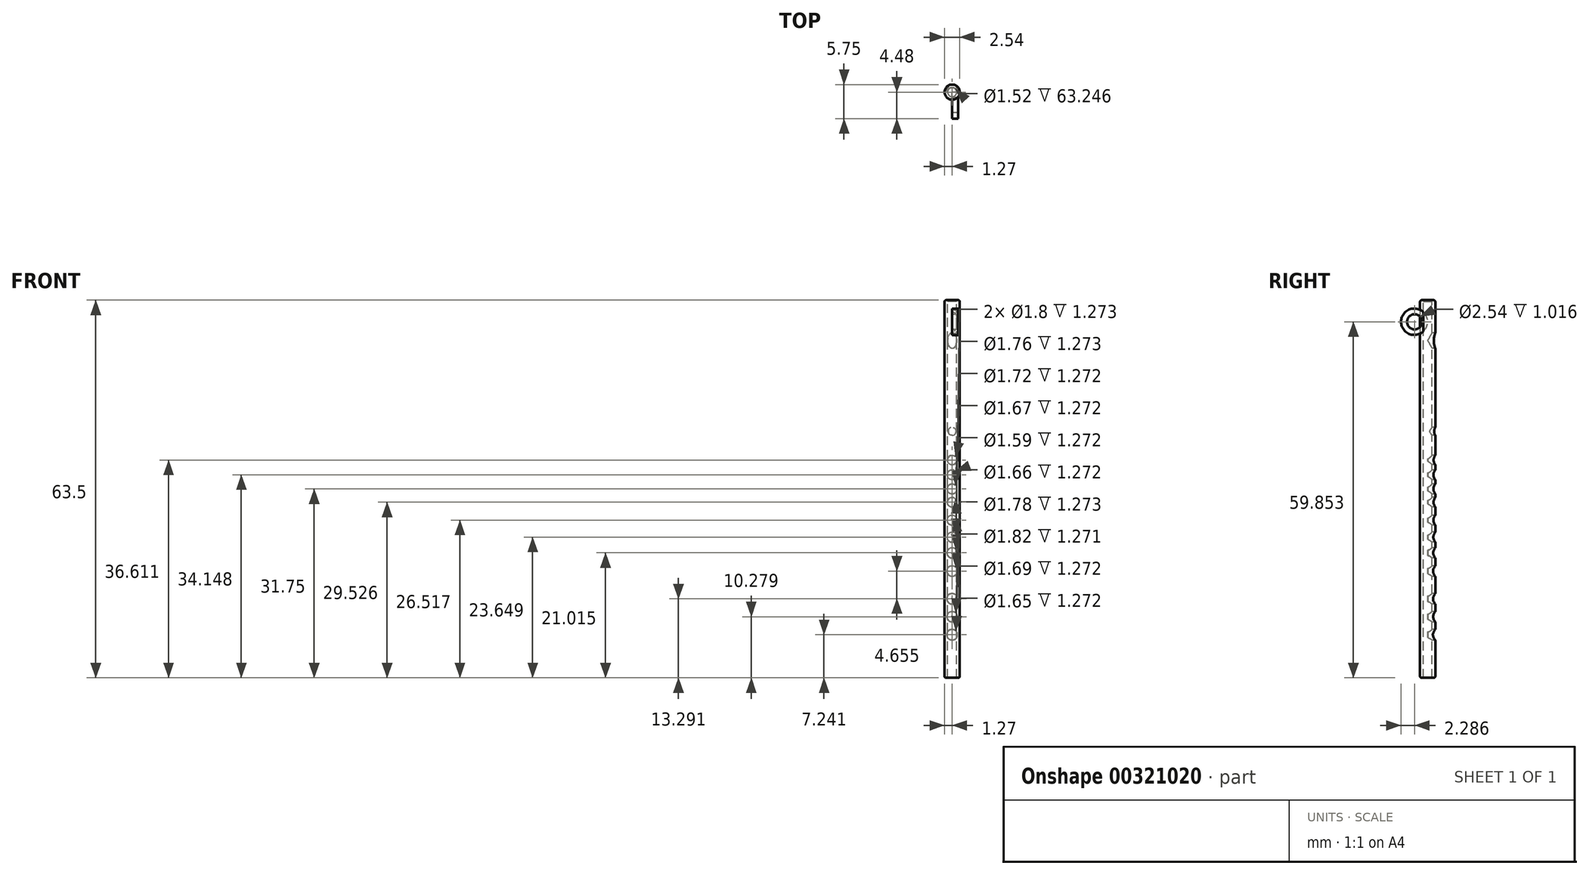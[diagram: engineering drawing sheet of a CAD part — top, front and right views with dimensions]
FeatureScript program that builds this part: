
annotation { "Feature Type Name" : "Feature", "Feature Type Description" : "" }
export const myFeature = defineFeature(function(context is Context, id is Id, definition is map)
    precondition{}
    {
        {
            var Q0;
            Q0=qCreatedBy(makeId("Top.planeOp"),FACE);
            var sketch = newSketch(context, id + "F0", { "sketchPlane" : qUnion([Q0])});
            skCircle(sketch, "E0", {"center": v(0, 0) * mm, "radius": 1.27 * mm});
            skSolve(sketch);
        }
        {
            var Q0;
            Q0 = qSketchRegion(id + "F0", true);
            extrude(context, id + "F1", {"entities" : qUnion([Q0]), "endBound" : BoundingType.SYMMETRIC, "depth" : 63.5 * mm});
        }
        {
            var Q0;
            Q0=makeQuery(id+"F1.opExtrude","CAP_FACE",FACE,{"disambiguationData":[OSD([sQuery(id+"F0.wireOp",EDGE,"E0")])],"isStart":false});
            var sketch = newSketch(context, id + "F2", { "sketchPlane" : qUnion([Q0])});
            skCircle(sketch, "E1", {"center": v(0, 0) * mm, "radius": 0.76 * mm});
            skSolve(sketch);
        }
        {
            var Q0;
            Q0=makeQuery(id+"F2.imprint","IMPRINT",FACE,{"disambiguationData":[TD([[makeQuery(id+"F2.imprint","IMPRINT",EDGE,{"derivedFrom":sQuery(id+"F2.wireOp",EDGE,"E1")}),1.0]])]});
            extrude(context, id + "F3", {"entities" : qUnion([Q0]), "operationType" : NewBodyOperationType.REMOVE, "endBound" : BoundingType.THROUGH_ALL, "oppositeDirection" : true, "depth" : 54.23 * mm});
        }
        {
            var Q0;
            Q0=qCreatedBy(makeId("Front.planeOp"),FACE);
            var sketch = newSketch(context, id + "F4", { "sketchPlane" : qUnion([Q0])});
            skLineSegment(sketch, "E2", {"start": v(0, 0) * mm, "end": v(0, 31.67) * mm, "construction": true});
            skLineSegment(sketch, "E3", {"start": v(0, 0) * mm, "end": v(0, -31.08) * mm, "construction": true});
            skEllipse(sketch, "E4", {"center": v(0, 24.95) * mm, "majorRadius": 1.32 * mm, "minorRadius": 0.76 * mm, "majorAxis": v(0, -1)});
            skCircle(sketch, "E5", {"center": v(0, -18.46) * mm, "radius": 0.9 * mm});
            skCircle(sketch, "E6", {"center": v(0, -21.47) * mm, "radius": 0.9 * mm});
            skCircle(sketch, "E7", {"center": v(0, 2.4) * mm, "radius": 0.83 * mm});
            skCircle(sketch, "E8", {"center": v(0, 9.7) * mm, "radius": 0.67 * mm});
            skCircle(sketch, "E9", {"center": v(0, 4.86) * mm, "radius": 0.8 * mm});
            skCircle(sketch, "E10", {"center": v(0, 0) * mm, "radius": 0.83 * mm});
            skCircle(sketch, "E11", {"center": v(0, -8.1) * mm, "radius": 0.86 * mm});
            skCircle(sketch, "E12", {"center": v(0, -10.74) * mm, "radius": 0.88 * mm});
            skCircle(sketch, "E13", {"center": v(0, -13.8) * mm, "radius": 0.9 * mm});
            skCircle(sketch, "E14", {"center": v(0, -2.22) * mm, "radius": 0.82 * mm});
            skCircle(sketch, "E15", {"center": v(0, -5.23) * mm, "radius": 0.85 * mm});
            skCircle(sketch, "E16", {"center": v(0, -24.5) * mm, "radius": 0.91 * mm});
            skSolve(sketch);
        }
        {
            var Q0;
            Q0 = qSketchRegion(id + "F4", true);
            extrude(context, id + "F5", {"entities" : qUnion([Q0]), "operationType" : NewBodyOperationType.REMOVE, "oppositeDirection" : true, "depth" : 25.4 * mm});
        }
        {
            var Q0;
            Q0 = qSketchRegion(id + "F2", true);
            extrude(context, id + "F6", {"entities" : qUnion([Q0]), "operationType" : NewBodyOperationType.ADD, "oppositeDirection" : true, "depth" : 0.25 * mm});
        }
        {
            var Q0;
            Q0=makeQuery(id+"F1.opExtrude","CAP_EDGE",EDGE,{"disambiguationData":[OSD([sQuery(id+"F0.wireOp",EDGE,"E0")])],"isStart":false});
            fillet(context, id + "F7", {"entities" : qUnion([Q0]), "radius" : 0.25 * mm, "tangentPropagation" : true, "allowEdgeOverflow" : false});
        }
        {
            var Q0;
            Q0=makeQuery(id+"F1.opExtrude","CAP_EDGE",EDGE,{"disambiguationData":[OSD([sQuery(id+"F0.wireOp",EDGE,"E0")])],"isStart":true});
            fillet(context, id + "F8", {"entities" : qUnion([Q0]), "radius" : 0.25 * mm, "tangentPropagation" : true, "allowEdgeOverflow" : false});
        }
        {
            var Q0;
            Q0=qCreatedBy(makeId("Right.planeOp"),FACE);
            var sketch = newSketch(context, id + "F9", { "sketchPlane" : qUnion([Q0])});
            skCircle(sketch, "E17", {"center": v(-2.26, 28.12) * mm, "radius": 2.22 * mm});
            skSolve(sketch);
        }
        {
            var Q0;
            Q0 = qSketchRegion(id + "F9", true);
            extrude(context, id + "F10", {"entities" : qUnion([Q0]), "operationType" : NewBodyOperationType.ADD, "depth" : 1.02 * mm});
        }
        {
            var Q0;
            Q0=qCreatedBy(makeId("Right.planeOp"),FACE);
            var sketch = newSketch(context, id + "F11", { "sketchPlane" : qUnion([Q0])});
            skCircle(sketch, "E18", {"center": v(-2.2, 28.1) * mm, "radius": 1.27 * mm});
            skSolve(sketch);
        }
        {
            var Q0;
            Q0 = qSketchRegion(id + "F11", true);
            extrude(context, id + "F12", {"entities" : qUnion([Q0]), "operationType" : NewBodyOperationType.REMOVE, "depth" : 13.16 * mm});
        }
    });
